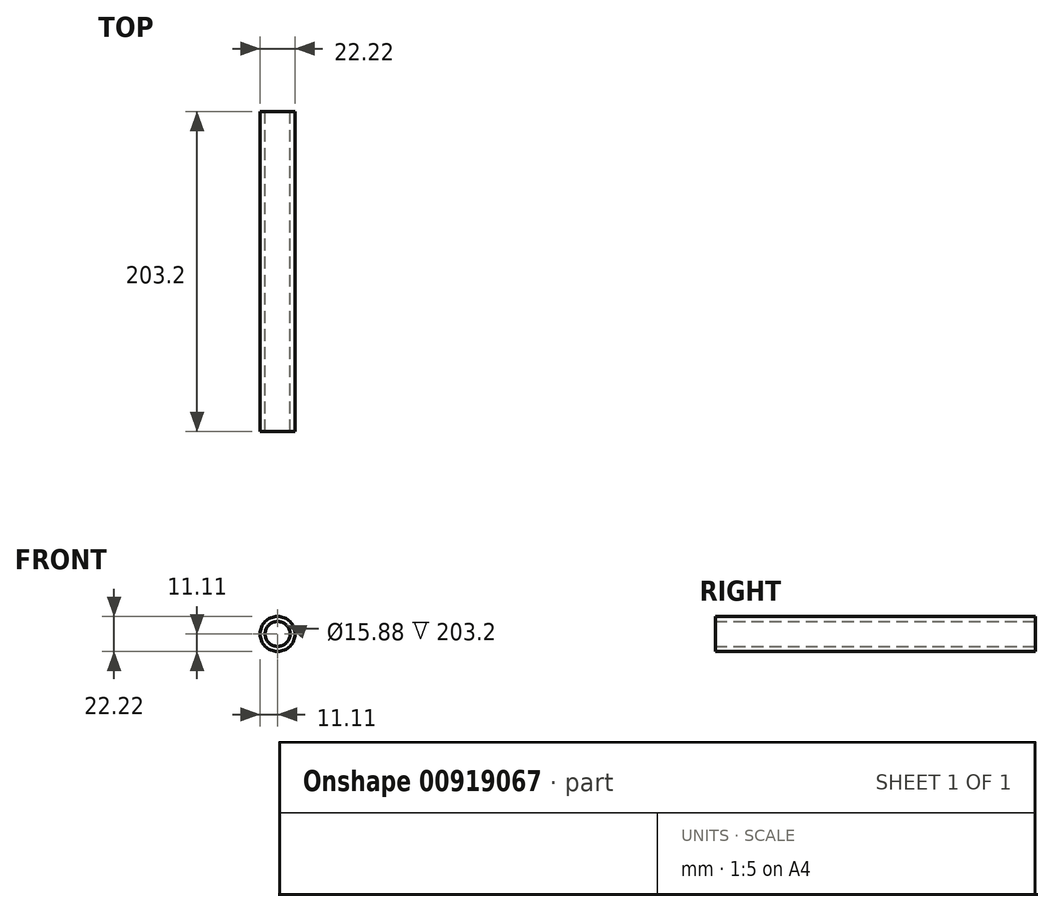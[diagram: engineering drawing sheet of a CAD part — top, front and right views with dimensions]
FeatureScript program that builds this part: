
annotation { "Feature Type Name" : "Feature", "Feature Type Description" : "" }
export const myFeature = defineFeature(function(context is Context, id is Id, definition is map)
    precondition{}
    {
        {
            var Q0;
            Q0=qCreatedBy(makeId("Front.planeOp"),FACE);
            var sketch = newSketch(context, id + "F0", { "sketchPlane" : qUnion([Q0])});
            skCircle(sketch, "E0", {"center": v(0, 0) * mm, "radius": 11.11 * mm});
            skCircle(sketch, "E1", {"center": v(0, 0) * mm, "radius": 7.94 * mm});
            skSolve(sketch);
        }
        {
            var Q0;
            Q0=makeQuery(id+"F0.imprint","IMPRINT",FACE,{"disambiguationData":[TD([[makeQuery(id+"F0.imprint","IMPRINT",EDGE,{"derivedFrom":sQuery(id+"F0.wireOp",EDGE,"E0")}),1.0]])]});
            extrude(context, id + "F1", {"entities" : qUnion([Q0]), "endBound" : BoundingType.SYMMETRIC, "depth" : 203.2 * mm, "offsetDistance" : 25.4 * mm});
        }
    });
